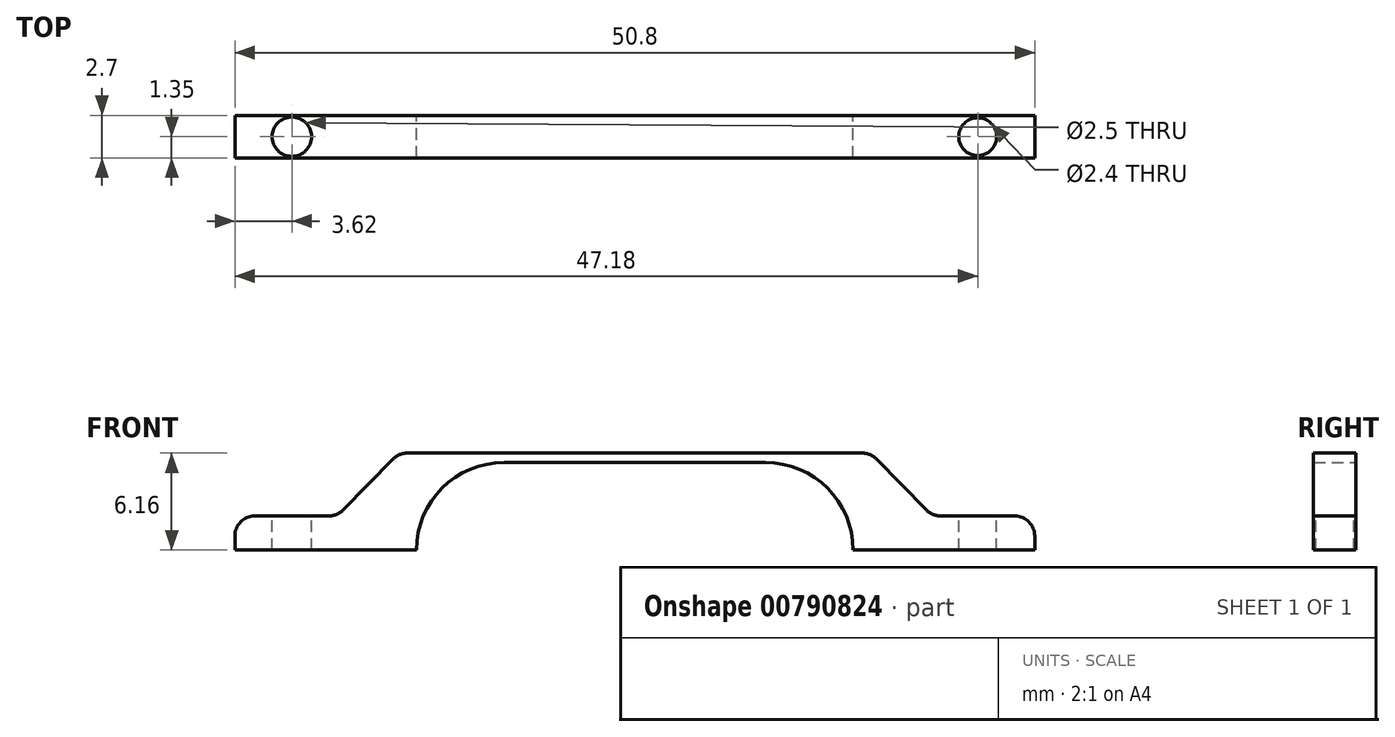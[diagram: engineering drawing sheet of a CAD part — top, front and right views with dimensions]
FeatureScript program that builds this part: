
annotation { "Feature Type Name" : "Feature", "Feature Type Description" : "" }
export const myFeature = defineFeature(function(context is Context, id is Id, definition is map)
    precondition{}
    {
        {
            var Q0;
            Q0=qCreatedBy(makeId("Front.planeOp"),FACE);
            var sketch = newSketch(context, id + "F0", { "sketchPlane" : qUnion([Q0])});
            skLineSegment(sketch, "E0", {"start": v(0, 0) * mm, "end": v(11.53, 0) * mm});
            skLineSegment(sketch, "E1", {"start": v(11.53, 0) * mm, "end": v(11.53, 0) * mm});
            skLineSegment(sketch, "E2", {"start": v(17.1, 5.56) * mm, "end": v(33.7, 5.56) * mm});
            skLineSegment(sketch, "E3", {"start": v(39.27, 0) * mm, "end": v(39.27, 0) * mm});
            skLineSegment(sketch, "E4", {"start": v(39.27, 0) * mm, "end": v(50.8, 0) * mm});
            skArc(sketch, "E5.filletArc", {"start": v(17.1, 5.56) * mm, "mid": v(13.16, 3.93) * mm, "end": v(11.53, 0) * mm});
            skArc(sketch, "E6.filletArc", {"start": v(39.27, 0) * mm, "mid": v(37.64, 3.93) * mm, "end": v(33.7, 5.56) * mm});
            skLineSegment(sketch, "E7", {"start": v(0, 0) * mm, "end": v(0, 2.16) * mm});
            skLineSegment(sketch, "E8", {"start": v(10.43, 6.16) * mm, "end": v(40.37, 6.16) * mm});
            skLineSegment(sketch, "E9", {"start": v(50.8, 2.16) * mm, "end": v(50.8, 0) * mm});
            skLineSegment(sketch, "E10", {"start": v(0, 2.16) * mm, "end": v(6.5, 2.16) * mm});
            skLineSegment(sketch, "E11", {"start": v(6.5, 2.16) * mm, "end": v(10.43, 6.16) * mm});
            skLineSegment(sketch, "E12", {"start": v(25.4, 6.16) * mm, "end": v(25.4, 0) * mm, "construction": true});
            skLineSegment(sketch, "E13.MirrorCS", {"start": v(44.3, 2.16) * mm, "end": v(40.37, 6.16) * mm});
            skLineSegment(sketch, "E14.MirrorCS", {"start": v(50.8, 2.16) * mm, "end": v(44.3, 2.16) * mm});
            skPoint(sketch, "E15.orphan", {"position": v(0, 6.16) * mm});
            skPoint(sketch, "E16.orphan", {"position": v(50.8, 6.16) * mm});
            skSolve(sketch);
        }
        {
            var Q0;
            Q0=makeQuery(id+"F0.imprint","IMPRINT",FACE,{"disambiguationData":[TD([[makeQuery(id+"F0.imprint","IMPRINT",EDGE,{"derivedFrom":sQuery(id+"F0.wireOp",EDGE,"E0")}),1.0]])]});
            extrude(context, id + "F1", {"entities" : qUnion([Q0]), "depth" : 2.7 * mm, "offsetDistance" : 25.4 * mm});
        }
        {
            var Q0;
            Q0=makeQuery(id+"F1.opExtrude","SWEPT_EDGE",EDGE,{"disambiguationData":[OSD([sQuery(id+"F0.wireOp",EDGE,"E9"),sQuery(id+"F0.wireOp",EDGE,"E14.MirrorCS")])]});
            var Q1;
            Q1=makeQuery(id+"F1.opExtrude","SWEPT_EDGE",EDGE,{"disambiguationData":[OSD([sQuery(id+"F0.wireOp",EDGE,"E13.MirrorCS"),sQuery(id+"F0.wireOp",EDGE,"E14.MirrorCS")])]});
            var Q2;
            Q2=makeQuery(id+"F1.opExtrude","SWEPT_EDGE",EDGE,{"disambiguationData":[OSD([sQuery(id+"F0.wireOp",EDGE,"E8"),sQuery(id+"F0.wireOp",EDGE,"E13.MirrorCS")])]});
            var Q3;
            Q3=makeQuery(id+"F1.opExtrude","SWEPT_EDGE",EDGE,{"disambiguationData":[OSD([sQuery(id+"F0.wireOp",EDGE,"E8"),sQuery(id+"F0.wireOp",EDGE,"E11")])]});
            var Q4;
            Q4=makeQuery(id+"F1.opExtrude","SWEPT_EDGE",EDGE,{"disambiguationData":[OSD([sQuery(id+"F0.wireOp",EDGE,"E10"),sQuery(id+"F0.wireOp",EDGE,"E11")])]});
            var Q5;
            Q5=makeQuery(id+"F1.opExtrude","SWEPT_EDGE",EDGE,{"disambiguationData":[OSD([sQuery(id+"F0.wireOp",EDGE,"E7"),sQuery(id+"F0.wireOp",EDGE,"E10")])]});
            fillet(context, id + "F2", {"entities" : qUnion([Q0, Q1, Q2, Q3, Q4, Q5]), "radius" : 1.27 * mm, "tangentPropagation" : true, "allowEdgeOverflow" : false});
        }
        {
            var Q0;
            Q0=makeQuery(id+"F1.opExtrude","SWEPT_FACE",FACE,{"disambiguationData":[OSD([sQuery(id+"F0.wireOp",EDGE,"E10")])]});
            var sketch = newSketch(context, id + "F3", { "sketchPlane" : qUnion([Q0])});
            skCircle(sketch, "E17", {"center": v(3.62, -1.35) * mm, "radius": 1.25 * mm});
            skPoint(sketch, "E17.centerSnap0", {"position": v(5.97, -1.35) * mm});
            skPoint(sketch, "E17.centerSnap1", {"position": v(3.62, 0) * mm});
            skSolve(sketch);
        }
        {
            var Q0;
            Q0=makeQuery(id+"F1.opExtrude","SWEPT_FACE",FACE,{"disambiguationData":[OSD([sQuery(id+"F0.wireOp",EDGE,"E14.MirrorCS")])]});
            var sketch = newSketch(context, id + "F4", { "sketchPlane" : qUnion([Q0])});
            skCircle(sketch, "E18", {"center": v(47.18, -1.35) * mm, "radius": 1.2 * mm});
            skPoint(sketch, "E18.centerSnap0", {"position": v(49.53, -1.35) * mm});
            skPoint(sketch, "E18.centerSnap1", {"position": v(47.18, 0) * mm});
            skSolve(sketch);
        }
        {
            var Q0;
            Q0=makeQuery(id+"F3.imprint","IMPRINT",FACE,{"disambiguationData":[TD([[makeQuery(id+"F3.imprint","IMPRINT",EDGE,{"derivedFrom":sQuery(id+"F3.wireOp",EDGE,"E17")}),1.0]])]});
            extrude(context, id + "F5", {"entities" : qUnion([Q0]), "operationType" : NewBodyOperationType.REMOVE, "endBound" : BoundingType.THROUGH_ALL, "oppositeDirection" : true, "depth" : 25.4 * mm, "offsetDistance" : 25.4 * mm});
        }
        {
            var Q0;
            Q0=makeQuery(id+"F4.imprint","IMPRINT",FACE,{"disambiguationData":[TD([[makeQuery(id+"F4.imprint","IMPRINT",EDGE,{"derivedFrom":sQuery(id+"F4.wireOp",EDGE,"E18")}),1.0]])]});
            extrude(context, id + "F6", {"entities" : qUnion([Q0]), "operationType" : NewBodyOperationType.REMOVE, "endBound" : BoundingType.THROUGH_ALL, "oppositeDirection" : true, "depth" : 25.4 * mm, "offsetDistance" : 25.4 * mm});
        }
    });
